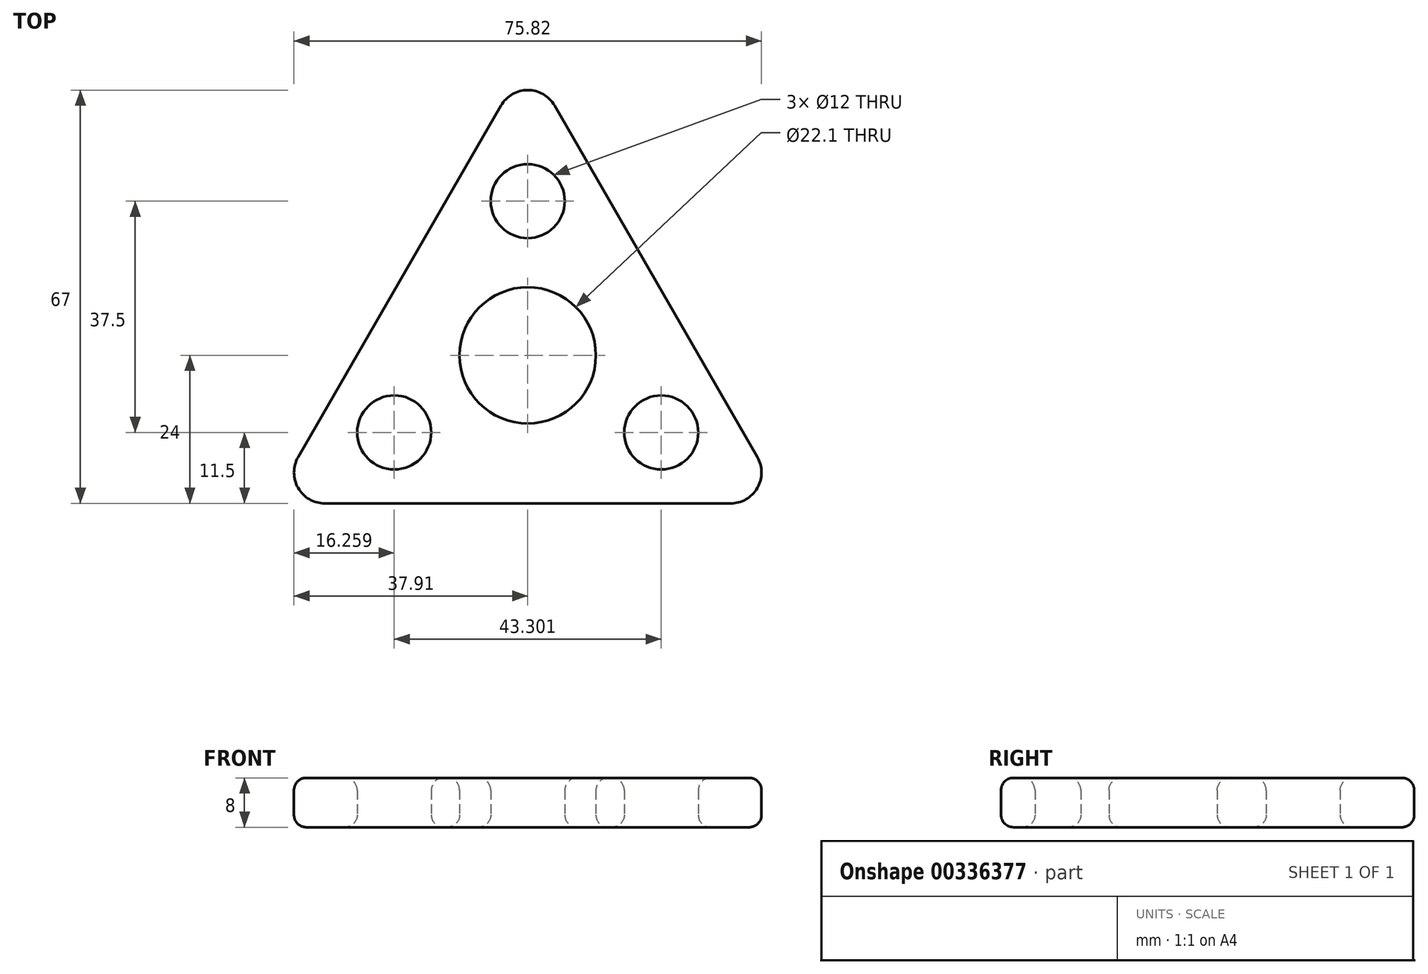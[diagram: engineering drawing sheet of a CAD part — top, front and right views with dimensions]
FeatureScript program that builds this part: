
annotation { "Feature Type Name" : "Feature", "Feature Type Description" : "" }
export const myFeature = defineFeature(function(context is Context, id is Id, definition is map)
    precondition{}
    {
        {
            var Q0;
            Q0=qCreatedBy(makeId("Top.planeOp"),FACE);
            var sketch = newSketch(context, id + "F0", { "sketchPlane" : qUnion([Q0])});
            skCircle(sketch, "E0", {"center": v(0, 0) * mm, "radius": 11.05 * mm});
            skLineSegment(sketch, "E1.0", {"start": v(41.57, -24) * mm, "end": v(-41.57, -24) * mm});
            skLineSegment(sketch, "E1.1", {"start": v(-41.57, -24) * mm, "end": v(0, 48) * mm});
            skLineSegment(sketch, "E1.2", {"start": v(0, 48) * mm, "end": v(41.57, -24) * mm});
            skPoint(sketch, "E1.0.midPoint", {"position": v(0, -24) * mm});
            skCircle(sketch, "E2", {"center": v(-21.65, -12.5) * mm, "radius": 6 * mm});
            skCircle(sketch, "E3.MirrorC", {"center": v(21.65, -12.5) * mm, "radius": 6 * mm});
            skCircle(sketch, "E4.MirrorC", {"center": v(0, 25) * mm, "radius": 6 * mm});
            skPoint(sketch, "E5.end.orphan", {"position": v(20.78, 12) * mm});
            skSolve(sketch);
        }
        {
            var Q0;
            Q0=makeQuery(id+"F0.imprint","IMPRINT",FACE,{"disambiguationData":[TD([[makeQuery(id+"F0.imprint","IMPRINT",EDGE,{"derivedFrom":sQuery(id+"F0.wireOp",EDGE,"E0")}),-1.0]])]});
            extrude(context, id + "F1", {"entities" : qUnion([Q0]), "depth" : 8 * mm, "offsetDistance" : 25 * mm});
        }
        {
            var Q0;
            Q0=makeQuery(id+"F1.opExtrude","CAP_FACE",FACE,{"disambiguationData":[OSD([sQuery(id+"F0.wireOp",EDGE,"E0"),sQuery(id+"F0.wireOp",EDGE,"E1.0"),sQuery(id+"F0.wireOp",EDGE,"E1.1"),sQuery(id+"F0.wireOp",EDGE,"E1.2"),sQuery(id+"F0.wireOp",EDGE,"E2"),sQuery(id+"F0.wireOp",EDGE,"E3.MirrorC"),sQuery(id+"F0.wireOp",EDGE,"E4.MirrorC")])],"isStart":false});
            var Q1;
            Q1=makeQuery(id+"F1.opExtrude","CAP_FACE",FACE,{"disambiguationData":[OSD([sQuery(id+"F0.wireOp",EDGE,"E0"),sQuery(id+"F0.wireOp",EDGE,"E1.0"),sQuery(id+"F0.wireOp",EDGE,"E1.1"),sQuery(id+"F0.wireOp",EDGE,"E1.2"),sQuery(id+"F0.wireOp",EDGE,"E2"),sQuery(id+"F0.wireOp",EDGE,"E3.MirrorC"),sQuery(id+"F0.wireOp",EDGE,"E4.MirrorC")])],"isStart":true});
            fillet(context, id + "F2", {"entities" : qUnion([Q0, Q1]), "tangentPropagation" : true, "radius" : 2 * mm, "defaultsChanged" : false, "vertexSettings" : [], "allowEdgeOverflow" : false});
        }
        {
            var Q0;
            Q0=makeQuery(id+"F1.opExtrude","SWEPT_EDGE",EDGE,{"disambiguationData":[OSD([sQuery(id+"F0.wireOp",EDGE,"E1.0"),sQuery(id+"F0.wireOp",EDGE,"E1.2")])]});
            var Q1;
            Q1=makeQuery(id+"F1.opExtrude","SWEPT_EDGE",EDGE,{"disambiguationData":[OSD([sQuery(id+"F0.wireOp",EDGE,"E1.0"),sQuery(id+"F0.wireOp",EDGE,"E1.1")])]});
            var Q2;
            Q2=makeQuery(id+"F1.opExtrude","SWEPT_EDGE",EDGE,{"disambiguationData":[OSD([sQuery(id+"F0.wireOp",EDGE,"E1.1"),sQuery(id+"F0.wireOp",EDGE,"E1.2")])]});
            fillet(context, id + "F3", {"entities" : qUnion([Q0, Q1, Q2]), "tangentPropagation" : true, "radius" : 5 * mm, "defaultsChanged" : false, "vertexSettings" : [], "allowEdgeOverflow" : false});
        }
    });
